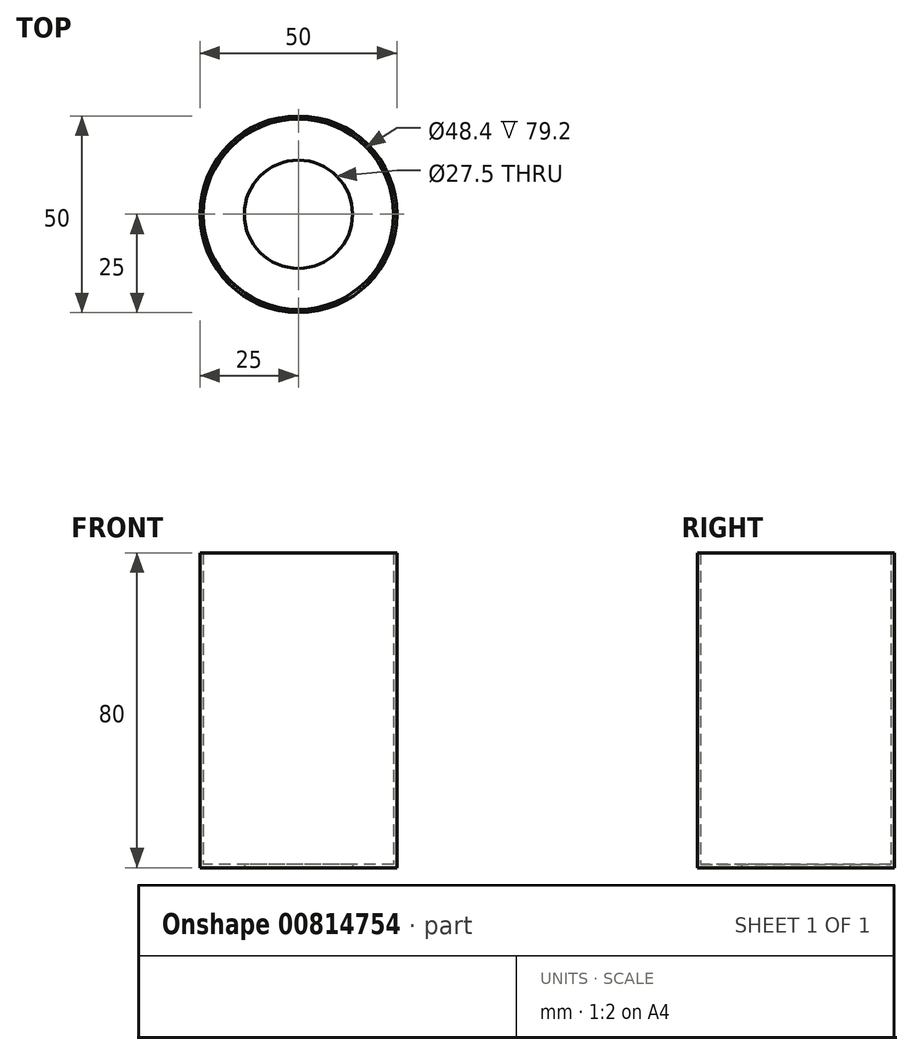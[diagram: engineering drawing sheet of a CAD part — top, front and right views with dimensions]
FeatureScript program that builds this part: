
annotation { "Feature Type Name" : "Feature", "Feature Type Description" : "" }
export const myFeature = defineFeature(function(context is Context, id is Id, definition is map)
    precondition{}
    {
        {
            var Q0;
            Q0=qCreatedBy(makeId("Top.planeOp"),FACE);
            var sketch = newSketch(context, id + "F0", { "sketchPlane" : qUnion([Q0])});
            skCircle(sketch, "E0", {"center": v(0, 0) * mm, "radius": 25 * mm});
            skSolve(sketch);
        }
        {
            var Q0;
            Q0=makeQuery(id+"F0.imprint","IMPRINT",FACE,{"disambiguationData":[TD([[makeQuery(id+"F0.imprint","IMPRINT",EDGE,{"derivedFrom":sQuery(id+"F0.wireOp",EDGE,"E0")}),1.0]])]});
            extrude(context, id + "F1", {"entities" : qUnion([Q0]), "depth" : 80 * mm, "offsetDistance" : 25 * mm});
        }
        {
            var Q0;
            Q0=makeQuery(id+"F1.opExtrude","CAP_FACE",FACE,{"disambiguationData":[OSD([sQuery(id+"F0.wireOp",EDGE,"E0")])],"isStart":true});
            var sketch = newSketch(context, id + "F2", { "sketchPlane" : qUnion([Q0])});
            skCircle(sketch, "E1", {"center": v(0, 0) * mm, "radius": 13.75 * mm});
            skSolve(sketch);
        }
        {
            var Q0;
            Q0=makeQuery(id+"F1.opExtrude","CAP_FACE",FACE,{"disambiguationData":[OSD([sQuery(id+"F0.wireOp",EDGE,"E0")])],"isStart":false});
            shell(context, id + "F3", {"entities" : qUnion([Q0]), "thickness" : 0.8 * mm});
        }
        {
            var Q0;
            Q0=makeQuery(id+"F2.imprint","IMPRINT",FACE,{"disambiguationData":[TD([[makeQuery(id+"F2.imprint","IMPRINT",EDGE,{"derivedFrom":sQuery(id+"F2.wireOp",EDGE,"E1")}),1.0]])]});
            extrude(context, id + "F4", {"entities" : qUnion([Q0]), "operationType" : NewBodyOperationType.REMOVE, "oppositeDirection" : true, "depth" : 25 * mm, "offsetDistance" : 25 * mm});
        }
    });
